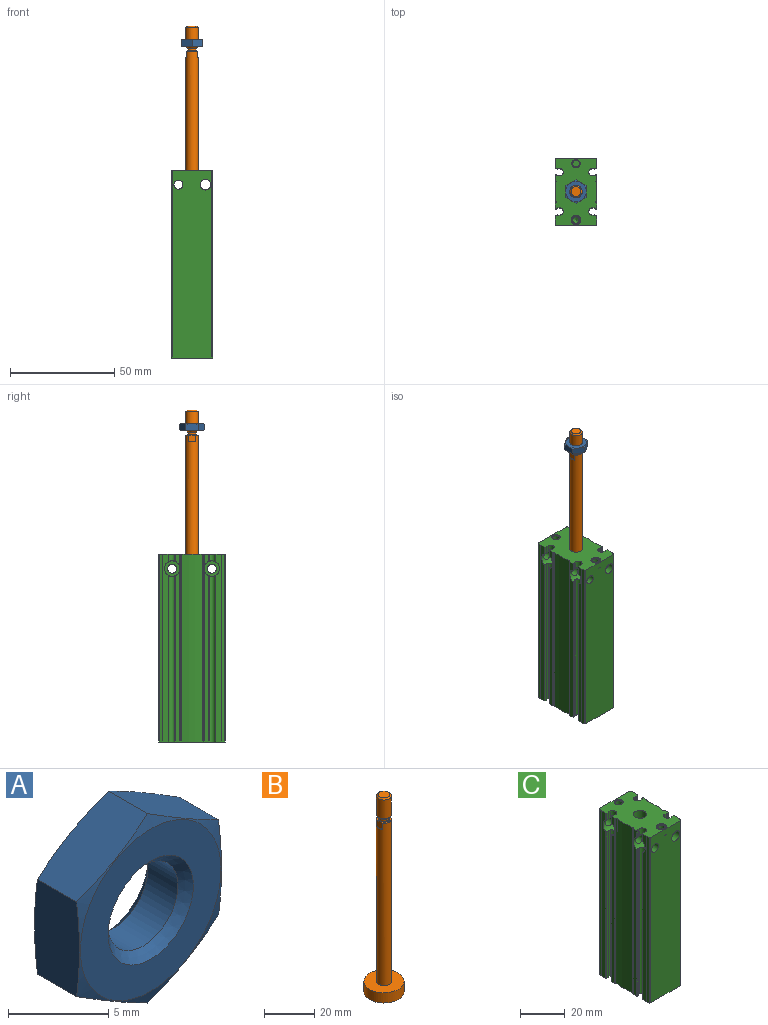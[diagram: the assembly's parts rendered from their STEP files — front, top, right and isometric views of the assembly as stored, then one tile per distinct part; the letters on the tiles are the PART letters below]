
ASSEMBLY  parts=3 mates=4
PART A: 13 faces, bbox 11.5x3.2x11.5 mm
  f0: plane 5.78x3.18mm, normal (-1,0,0), area 17.5mm2, adj f1,f2,f4,f8
  f1: plane 5x3.18mm, normal (-0.5,0,-0.87), area 17.5mm2, adj f0,f2,f8,f12
  f2: cone r=10.92mm half-angle=75deg, axis (0,1,0), area 10mm2, adj f0,f1,f3,f4,f5,f6,f12
  f3: plane 5.78x3.18mm, normal (1,0,0), area 17.5mm2, adj f2,f6,f8,f12
  f4: plane 5x3.18mm, normal (-0.5,0,0.87), area 17.5mm2, adj f0,f2,f6,f8
  f5: plane 9.9x9.9mm, normal (0,-1,0), area 48.7mm2, adj f2,f9
  f6: plane 5x3.18mm, normal (0.5,0,0.87), area 17.5mm2, adj f2,f3,f4,f8
  f7: plane 9.9x9.9mm, normal (0,1,0), area 48.7mm2, adj f8,f11
  f8: cone r=4.95mm half-angle=75deg, axis (0,-1,0), area 10mm2, adj f0,f1,f3,f4,f6,f7,f12
  f9: cone r=2.46mm half-angle=45deg, axis (0,-1,0), area 13.1mm2, adj f5,f10
  f10: cylinder r=2.46mm len=4.92mm, axis (0,1,0), area 32.7mm2, adj f9,f11
  f11: cone r=3mm half-angle=45deg, axis (0,1,0), area 13.1mm2, adj f7,f10
  f12: plane 5x3.18mm, normal (0.5,0,-0.87), area 17.5mm2, adj f1,f2,f3,f8
PART B: 16 faces, bbox 16x16x96.4 mm
  f0: torus R=2.2mm, axis (0,0,-1), area 4.1mm2, adj f1,f8
  f1: cylinder r=2mm len=4mm, axis (0,0,1), area 11.8mm2, adj f0,f2
  f2: torus R=2.2mm, axis (0,0,-1), area 2mm2, adj f1,f3
  f3: cone r=3mm half-angle=45deg, axis (0,0,1), area 21.2mm2, adj f2,f4
  f4: cylinder r=3mm len=9.16mm, axis (0,0,1), area 172.7mm2, adj f3,f5
  f5: cone r=2.39mm half-angle=45deg, axis (0,0,-1), area 14.7mm2, adj f4,f6
  f6: plane 4.77x4.77mm, normal (0,0,1), area 17.9mm2, adj f5
  f7: plane 16x16mm, normal (0,0,-1), area 201.1mm2, adj f11
  f8: plane 6x5mm, normal (0,0,1), area 10.8mm2, adj f0,f9,f12,f13
  f9: cylinder r=3mm len=79.4mm, axis (0,0,1), area 1475.6mm2, adj f8,f10,f12,f13,f14,f15
  f10: plane 16x16mm, normal (0,0,1), area 172.8mm2, adj f9,f11
  f11: cylinder r=8mm len=16mm, axis (0,0,1), area 251.3mm2, adj f7,f10
  f12: plane 3.32x3mm, normal (1,0,0), area 9.9mm2, adj f8,f9,f15
  f13: plane 3.32x3mm, normal (-1,0,0), area 9.9mm2, adj f8,f9,f14
  f14: plane 3.32x0.5mm, normal (0,0,1), area 1.1mm2, adj f9,f13
  f15: plane 3.32x0.5mm, normal (0,0,1), area 1.1mm2, adj f9,f12
PART C: 184 faces, bbox 20x32x90 mm
  f0: plane 7.43x3.25mm, normal (1,0,0), area 13.2mm2, adj f17,f79,f178,f180
  f1: plane 7.43x3.25mm, normal (1,0,0), area 13.2mm2, adj f23,f27,f178,f179
  f2: cylinder r=3.75mm len=7.5mm, axis (-1,0,0), area 83.1mm2, adj f3,f4,f5,f6,f7,f8,f9,f10
  f3: cylinder r=0.18mm len=79.59mm, axis (0,0,-1), area 22.5mm2, adj f2,f4,f92,f167
  f4: cylinder r=0.2mm len=79.71mm, axis (0,0,-1), area 26.5mm2, adj f2,f3,f5,f92
  f5: plane 79.76x0.95mm, normal (0.08,1,0), area 75.8mm2, adj f2,f4,f6,f92
  f6: cylinder r=1.8mm len=79.76mm, axis (0,0,-1), area 423.1mm2, adj f2,f5,f92,f157
  f7: plane 3.78x0.93mm, normal (-0.26,-0.96,0), area 3.5mm2, adj f2,f48,f134,f135
  f8: cylinder r=0.2mm len=79.77mm, axis (0,0,-1), area 26.5mm2, adj f2,f9,f92,f157
  f9: cylinder r=0.18mm len=79.68mm, axis (0,0,-1), area 22.5mm2, adj f2,f8,f92,f173
  f10: plane 3.71x1.07mm, normal (-0.17,-0.98,0), area 3.9mm2, adj f2,f48,f136,f174
  f11: cylinder r=0.2mm len=79.81mm, axis (0,0,-1), area 22.3mm2, adj f2,f62,f92,f173
  f12: cylinder r=6mm len=90mm, axis (0,0,-1), area 154.4mm2, adj f13,f48,f62,f92
  f13: cylinder r=0.43mm len=90mm, axis (0,0,-1), area 49.6mm2, adj f12,f48,f81,f92
  f14: cylinder r=0.43mm len=90mm, axis (0,0,-1), area 49.6mm2, adj f15,f48,f81,f92
  f15: cylinder r=6mm len=90mm, axis (0,0,-1), area 154.4mm2, adj f14,f48,f92,f110
  f16: cylinder r=0.2mm len=79.81mm, axis (0,0,-1), area 22.3mm2, adj f17,f74,f92,f110
  f17: cylinder r=3.75mm len=7.5mm, axis (-1,0,0), area 72.2mm2, adj f0,f16,f18,f19,f20,f21,f52,f66
  f18: cylinder r=3.75mm len=0.07mm, axis (-1,0,0), area 0mm2, adj f17,f21
  f19: cylinder r=0.18mm len=79.59mm, axis (0,0,-1), area 22.5mm2, adj f17,f20,f76,f92
  f20: plane 79.51x0.47mm, normal (-0.17,0.98,0), area 37.9mm2, adj f17,f19,f21,f92
  f21: cylinder r=0.2mm len=79.55mm, axis (0,0,-1), area 27.8mm2, adj f17,f18,f20,f66,f92
  f22: cylinder r=0.2mm len=79.55mm, axis (0,0,-1), area 27.8mm2, adj f23,f24,f92,f93,f139
  f23: cylinder r=3.75mm len=7.5mm, axis (-1,0,0), area 72.2mm2, adj f1,f22,f24,f57,f64,f93,f109,f111
  f24: cylinder r=3.75mm len=0.07mm, axis (-1,0,0), area 0mm2, adj f22,f23
  f25: cone r=2mm half-angle=60deg, axis (0,0,1), area 14.5mm2, adj f26
  f26: cylinder r=2mm len=53.5mm, axis (0,0,1), area 670.4mm2, adj f25,f27,f42
  f27: cylinder r=2.15mm len=8mm, axis (-1,0,0), area 106.1mm2, adj f1,f26,f28,f177,f178,f179
  f28: plane 7.5x7.5mm, normal (-1,0,0), area 29.7mm2, adj f27,f29
  f29: cylinder r=3.75mm len=7.5mm, axis (-1,0,0), area 83.1mm2, adj f28,f30,f31,f32,f33,f34,f35,f36
  f30: cylinder r=0.18mm len=79.59mm, axis (0,0,-1), area 22.5mm2, adj f29,f92,f125,f127
  f31: cylinder r=0.2mm len=79.55mm, axis (0,0,-1), area 27.8mm2, adj f29,f63,f92,f127
  f32: cylinder r=0.2mm len=79.81mm, axis (0,0,-1), area 22.3mm2, adj f29,f61,f92,f132
  f33: cylinder r=0.18mm len=79.68mm, axis (0,0,-1), area 22.5mm2, adj f29,f34,f92,f132
  f34: cylinder r=0.2mm len=79.77mm, axis (0,0,-1), area 26.5mm2, adj f29,f33,f39,f92
  f35: cylinder r=1.8mm len=79.76mm, axis (0,0,-1), area 423.1mm2, adj f29,f39,f92,f123
  f36: cylinder r=2.15mm len=4.3mm, axis (0,1,0), area 46.3mm2, adj f29,f60
  f37: cylinder r=2.15mm len=12.86mm, axis (0,1,0), area 173.7mm2, adj f2,f29
  f38: cylinder r=2.15mm len=4.3mm, axis (0,1,0), area 46.3mm2, adj f2,f81
  f39: plane 79.78x0.93mm, normal (-0.26,0.96,0), area 75.8mm2, adj f29,f34,f35,f92
  f40: plane 4.05x4.05mm, normal (0,0,1), area 3.3mm2, adj f41,f45
  f41: cone r=1.75mm half-angle=45deg, axis (0,0,1), area 3.6mm2, adj f40,f44
  f42: plane 4x4mm, normal (0,0,-1), area 2.9mm2, adj f26,f43
  f43: cone r=1.5mm half-angle=45deg, axis (0,0,-1), area 3.6mm2, adj f42,f44
  f44: cylinder r=1.5mm len=3mm, axis (0,0,1), area 28.3mm2, adj f41,f43
  f45: cone r=2.27mm half-angle=45deg, axis (0,0,-1), area 4.3mm2, adj f40,f46
  f46: cylinder r=2.25mm len=4.5mm, axis (0,0,1), area 0.4mm2, adj f45,f47
  f47: cone r=2.37mm half-angle=30deg, axis (0,0,1), area 3.3mm2, adj f46,f48
  f48: plane 32x20mm, normal (0,0,1), area 524.9mm2, adj f7,f10,f12,f13,f14,f15,f47,f49
  f49: cylinder r=3mm len=17.4mm, axis (0,0,1), area 328mm2, adj f48,f50
  f50: plane 16x16mm, normal (0,0,-1), area 172.8mm2, adj f49,f91
  f51: plane 90x0.28mm, normal (0.77,0.64,0), area 32.3mm2, adj f48,f56,f57,f92
  f52: cylinder r=0.2mm len=90mm, axis (0,0,-1), area 12.5mm2, adj f17,f48,f53,f66,f92,f108
  f53: plane 90x0.28mm, normal (0.77,-0.64,0), area 32.3mm2, adj f48,f52,f54,f92
  f54: cylinder r=0.75mm len=90mm, axis (0,0,-1), area 54mm2, adj f48,f53,f55,f92
  f55: cylinder r=47.5mm len=90mm, axis (0,0,-1), area 876.4mm2, adj f48,f54,f56,f92
  f56: cylinder r=0.75mm len=90mm, axis (0,0,-1), area 54mm2, adj f48,f51,f55,f92
  f57: cylinder r=0.2mm len=90mm, axis (0,0,-1), area 12.5mm2, adj f23,f48,f51,f64,f92,f93
  f58: cylinder r=0.2mm len=90mm, axis (0,0,-1), area 12.5mm2, adj f29,f48,f59,f63,f92,f166
  f59: plane 6.26x2.2mm, normal (-1,0,0), area 9.8mm2, adj f29,f48,f58,f128
  f60: plane 90x18.69mm, normal (0,-1,0), area 1647.2mm2, adj f36,f48,f92,f117,f118,f179
  f61: plane 90x2.52mm, normal (-1,0,0), area 219mm2, adj f29,f32,f48,f92,f119,f121
  f62: plane 90x2.52mm, normal (-1,0,0), area 219mm2, adj f2,f11,f12,f48,f92,f174
  f63: plane 82.26x2.2mm, normal (-1,0,0), area 177.3mm2, adj f29,f31,f58,f92
  f64: plane 6.26x2.2mm, normal (1,0,0), area 9.8mm2, adj f23,f48,f57,f133
  f65: plane 6.26x2.2mm, normal (-1,0,0), area 9.8mm2, adj f2,f48,f159,f161
  f66: plane 82.26x2.2mm, normal (1,0,0), area 177.3mm2, adj f17,f21,f52,f92
  f67: cylinder r=0.18mm len=3.68mm, axis (0,0,-1), area 1mm2, adj f17,f48,f138,f168
  f68: cylinder r=0.18mm len=79.68mm, axis (0,0,-1), area 22.5mm2, adj f17,f69,f74,f92
  f69: cylinder r=0.2mm len=79.77mm, axis (0,0,-1), area 26.5mm2, adj f17,f68,f70,f92
  f70: plane 79.78x0.93mm, normal (0.26,-0.96,0), area 75.8mm2, adj f17,f69,f71,f92
  f71: cylinder r=1.8mm len=79.76mm, axis (0,0,-1), area 423.6mm2, adj f17,f70,f72,f92
  f72: plane 79.76x0.95mm, normal (-0.08,1,0), area 75.8mm2, adj f17,f71,f76,f92
  f73: plane 3.76x0.95mm, normal (-0.08,1,0), area 3.6mm2, adj f17,f48,f75,f137
  f74: plane 79.71x1.07mm, normal (0.17,-0.98,0), area 85.8mm2, adj f16,f17,f68,f92
  f75: cylinder r=0.2mm len=3.71mm, axis (0,0,-1), area 1.2mm2, adj f17,f48,f73,f77
  f76: cylinder r=0.2mm len=79.71mm, axis (0,0,-1), area 26.5mm2, adj f17,f19,f72,f92
  f77: cylinder r=0.18mm len=3.59mm, axis (0,0,-1), area 1mm2, adj f17,f48,f75,f175
  f78: plane 7.43x3.25mm, normal (1,0,0), area 13.2mm2, adj f17,f79,f178,f180
  f79: cylinder r=2.15mm len=8mm, axis (-1,0,0), area 108.1mm2, adj f0,f78,f80,f178,f180
  f80: plane 7.5x7.5mm, normal (-1,0,0), area 29.7mm2, adj f2,f79
  f81: plane 90x18.69mm, normal (0,1,0), area 1607.9mm2, adj f13,f14,f38,f48,f82,f92,f99,f180
  f82: cone r=2.5mm half-angle=45deg, axis (0,1,0), area 8.8mm2, adj f81,f83
  f83: cylinder r=2.07mm len=5.57mm, axis (0,1,0), area 72.3mm2, adj f82,f100
  f84: plane 13.4x13.4mm, normal (0,0,-1), area 141mm2, adj f86
  f85: cone r=9.4mm half-angle=45deg, axis (0,0,-1), area 32.7mm2, adj f89,f92
  f86: cone r=7mm half-angle=45deg, axis (0,0,1), area 18.3mm2, adj f84,f87
  f87: cylinder r=7mm len=14mm, axis (0,0,1), area 79.2mm2, adj f86,f88
  f88: plane 18x18mm, normal (0,0,-1), area 100.5mm2, adj f87,f89
  f89: cylinder r=9mm len=18mm, axis (0,0,1), area 96.1mm2, adj f85,f88
  f90: plane 16x16mm, normal (0,0,1), area 201.1mm2, adj f91
  f91: cylinder r=8mm len=55mm, axis (0,0,1), area 2764.6mm2, adj f50,f90
  f92: plane 32x20mm, normal (0,0,-1), area 280.5mm2, adj f3,f4,f5,f6,f8,f9,f11,f12
  f93: plane 82.26x2.2mm, normal (1,0,0), area 177.3mm2, adj f22,f23,f57,f92
  f94: cone r=1.62mm half-angle=45deg, axis (0,0,-1), area 6.1mm2, adj f92,f95
  f95: cylinder r=1.62mm len=7.12mm, axis (0,0,1), area 72.5mm2, adj f94,f96
  f96: plane 3.24x3.24mm, normal (0,0,-1), area 8.3mm2, adj f95
  f97: plane 4.13x4.13mm, normal (0,1,0), area 13.4mm2, adj f98
  f98: cylinder r=2.07mm len=5.57mm, axis (0,1,0), area 72.3mm2, adj f97,f99
  f99: cone r=2.5mm half-angle=45deg, axis (0,1,0), area 8.8mm2, adj f81,f98
  f100: plane 4.13x4.13mm, normal (0,1,0), area 13.4mm2, adj f83
  f101: plane 3.24x3.24mm, normal (0,0,-1), area 8.3mm2, adj f102
  f102: cylinder r=1.62mm len=7.12mm, axis (0,0,1), area 72.5mm2, adj f101,f103
  f103: cone r=1.62mm half-angle=45deg, axis (0,0,-1), area 6.1mm2, adj f92,f102
  f104: cone r=2mm half-angle=45deg, axis (0,0,1), area 6.1mm2, adj f48,f105
  f105: cylinder r=1.62mm len=7.12mm, axis (0,0,1), area 72.5mm2, adj f104,f106
  f106: plane 3.24x3.24mm, normal (0,0,1), area 8.3mm2, adj f105
  f107: plane 82.26x2.2mm, normal (-1,0,0), area 177.3mm2, adj f2,f92,f158,f161
  f108: plane 6.26x2.2mm, normal (1,0,0), area 9.8mm2, adj f17,f48,f52,f176
  f109: plane 90x2.52mm, normal (1,0,0), area 219mm2, adj f23,f48,f92,f113,f116,f120
  f110: plane 90x2.52mm, normal (1,0,0), area 219mm2, adj f15,f16,f17,f48,f92,f160
  f111: plane 79.71x1.07mm, normal (0.17,0.98,0), area 85.8mm2, adj f23,f92,f120,f147
  f112: plane 79.78x0.93mm, normal (0.26,0.96,0), area 75.8mm2, adj f23,f92,f145,f146
  f113: cylinder r=6mm len=90mm, axis (0,0,-1), area 154.4mm2, adj f48,f92,f109,f118
  f114: plane 3.71x1.07mm, normal (0.17,0.98,0), area 3.9mm2, adj f23,f48,f116,f148
  f115: plane 79.76x0.95mm, normal (-0.08,-1,0), area 75.8mm2, adj f23,f92,f143,f145
  f116: cylinder r=0.2mm len=3.81mm, axis (0,0,-1), area 1mm2, adj f23,f48,f109,f114
  f117: cylinder r=0.43mm len=90mm, axis (0,0,-1), area 49.6mm2, adj f48,f60,f92,f119
  f118: cylinder r=0.43mm len=90mm, axis (0,0,-1), area 49.6mm2, adj f48,f60,f92,f113
  f119: cylinder r=6mm len=90mm, axis (0,0,-1), area 154.4mm2, adj f48,f61,f92,f117
  f120: cylinder r=0.2mm len=79.81mm, axis (0,0,-1), area 22.3mm2, adj f23,f92,f109,f111
  f121: cylinder r=0.2mm len=3.81mm, axis (0,0,-1), area 1mm2, adj f29,f48,f61,f122
  f122: plane 3.71x1.07mm, normal (-0.17,0.98,0), area 3.9mm2, adj f29,f48,f121,f149
  f123: plane 79.76x0.95mm, normal (0.08,-1,0), area 75.8mm2, adj f29,f35,f92,f125
  f124: cylinder r=0.2mm len=3.71mm, axis (0,0,-1), area 1.2mm2, adj f29,f48,f126,f130
  f125: cylinder r=0.2mm len=79.71mm, axis (0,0,-1), area 26.5mm2, adj f29,f30,f92,f123
  f126: cylinder r=0.18mm len=3.59mm, axis (0,0,-1), area 1mm2, adj f29,f48,f124,f129
  f127: plane 79.51x0.47mm, normal (0.17,-0.98,0), area 37.9mm2, adj f29,f30,f31,f92
  f128: cylinder r=0.2mm len=3.55mm, axis (0,0,-1), area 1.2mm2, adj f29,f48,f59,f129
  f129: plane 3.51x0.47mm, normal (0.17,-0.98,0), area 1.7mm2, adj f29,f48,f126,f128
  f130: plane 3.76x0.95mm, normal (0.08,-1,0), area 3.6mm2, adj f29,f48,f124,f151
  f131: plane 3.78x0.93mm, normal (-0.26,0.96,0), area 3.5mm2, adj f29,f48,f150,f151
  f132: plane 79.71x1.07mm, normal (-0.17,0.98,0), area 85.8mm2, adj f29,f32,f33,f92
  f133: cylinder r=0.2mm len=3.55mm, axis (0,0,-1), area 1.2mm2, adj f23,f48,f64,f154
  f134: cylinder r=1.8mm len=3.76mm, axis (0,0,-1), area 19.7mm2, adj f2,f7,f48,f172
  f135: cylinder r=0.2mm len=3.77mm, axis (0,0,-1), area 1.2mm2, adj f2,f7,f48,f136
  f136: cylinder r=0.18mm len=3.68mm, axis (0,0,-1), area 1mm2, adj f2,f10,f48,f135
  f137: cylinder r=1.8mm len=3.76mm, axis (0,0,-1), area 19.7mm2, adj f17,f48,f73,f156
  f138: cylinder r=0.2mm len=3.77mm, axis (0,0,-1), area 1.2mm2, adj f17,f48,f67,f156
  f139: plane 79.51x0.47mm, normal (-0.17,-0.98,0), area 37.9mm2, adj f22,f23,f92,f141
  f140: cylinder r=0.18mm len=3.59mm, axis (0,0,-1), area 1mm2, adj f23,f48,f142,f154
  f141: cylinder r=0.18mm len=79.59mm, axis (0,0,-1), area 22.5mm2, adj f23,f92,f139,f143
  f142: cylinder r=0.2mm len=3.71mm, axis (0,0,-1), area 1.2mm2, adj f23,f48,f140,f144
  f143: cylinder r=0.2mm len=79.71mm, axis (0,0,-1), area 26.5mm2, adj f23,f92,f115,f141
  f144: plane 3.76x0.95mm, normal (-0.08,-1,0), area 3.6mm2, adj f23,f48,f142,f153
  f145: cylinder r=1.8mm len=79.76mm, axis (0,0,-1), area 423.6mm2, adj f23,f92,f112,f115
  f146: cylinder r=0.2mm len=79.77mm, axis (0,0,-1), area 26.5mm2, adj f23,f92,f112,f147
  f147: cylinder r=0.18mm len=79.68mm, axis (0,0,-1), area 22.5mm2, adj f23,f92,f111,f146
  f148: cylinder r=0.18mm len=3.68mm, axis (0,0,-1), area 1mm2, adj f23,f48,f114,f152
  f149: cylinder r=0.18mm len=3.68mm, axis (0,0,-1), area 1mm2, adj f29,f48,f122,f150
  f150: cylinder r=0.2mm len=3.77mm, axis (0,0,-1), area 1.2mm2, adj f29,f48,f131,f149
  f151: cylinder r=1.8mm len=3.76mm, axis (0,0,-1), area 19.7mm2, adj f29,f48,f130,f131
  f152: cylinder r=0.2mm len=3.77mm, axis (0,0,-1), area 1.2mm2, adj f23,f48,f148,f155
  f153: cylinder r=1.8mm len=3.76mm, axis (0,0,-1), area 19.7mm2, adj f23,f48,f144,f155
  f154: plane 3.51x0.47mm, normal (-0.17,-0.98,0), area 1.7mm2, adj f23,f48,f133,f140
  f155: plane 3.78x0.93mm, normal (0.26,0.96,0), area 3.5mm2, adj f23,f48,f152,f153
  f156: plane 3.78x0.93mm, normal (0.26,-0.96,0), area 3.5mm2, adj f17,f48,f137,f138
  f157: plane 79.78x0.93mm, normal (-0.26,-0.96,0), area 75.8mm2, adj f2,f6,f8,f92
  f158: cylinder r=0.2mm len=79.55mm, axis (0,0,-1), area 27.8mm2, adj f2,f92,f107,f167
  f159: cylinder r=0.2mm len=3.55mm, axis (0,0,-1), area 1.2mm2, adj f2,f48,f65,f169
  f160: cylinder r=0.2mm len=3.81mm, axis (0,0,-1), area 1mm2, adj f17,f48,f110,f168
  f161: cylinder r=0.2mm len=90mm, axis (0,0,-1), area 12.5mm2, adj f2,f48,f65,f92,f107,f162
  f162: plane 90x0.28mm, normal (-0.77,-0.64,0), area 32.3mm2, adj f48,f92,f161,f163
  f163: cylinder r=0.75mm len=90mm, axis (0,0,-1), area 54mm2, adj f48,f92,f162,f164
  f164: cylinder r=47.5mm len=90mm, axis (0,0,-1), area 876.4mm2, adj f48,f92,f163,f165
  f165: cylinder r=0.75mm len=90mm, axis (0,0,-1), area 54mm2, adj f48,f92,f164,f166
  f166: plane 90x0.28mm, normal (-0.77,0.64,0), area 32.3mm2, adj f48,f58,f92,f165
  f167: plane 79.51x0.47mm, normal (0.17,0.98,0), area 37.9mm2, adj f2,f3,f92,f158
  f168: plane 3.71x1.07mm, normal (0.17,-0.98,0), area 3.9mm2, adj f17,f48,f67,f160
  f169: plane 3.51x0.47mm, normal (0.17,0.98,0), area 1.7mm2, adj f2,f48,f159,f170
  f170: cylinder r=0.18mm len=3.59mm, axis (0,0,-1), area 1mm2, adj f2,f48,f169,f171
  f171: cylinder r=0.2mm len=3.71mm, axis (0,0,-1), area 1.2mm2, adj f2,f48,f170,f172
  f172: plane 3.76x0.95mm, normal (0.08,1,0), area 3.6mm2, adj f2,f48,f134,f171
  f173: plane 79.71x1.07mm, normal (-0.17,-0.98,0), area 85.8mm2, adj f2,f9,f11,f92
  f174: cylinder r=0.2mm len=3.81mm, axis (0,0,-1), area 1mm2, adj f2,f10,f48,f62
  f175: plane 3.51x0.47mm, normal (-0.17,0.98,0), area 1.7mm2, adj f17,f48,f77,f176
  f176: cylinder r=0.2mm len=3.55mm, axis (0,0,-1), area 1.2mm2, adj f17,f48,f108,f175
  f177: plane 7.43x3.25mm, normal (1,0,0), area 13.2mm2, adj f23,f27,f178,f179
  f178: cylinder r=2.55mm len=14.82mm, axis (0,-1,0), area 203mm2, adj f0,f1,f17,f23,f27,f78,f79,f177
  f179: cylinder r=2.55mm len=5.1mm, axis (0,-1,0), area 53.3mm2, adj f1,f23,f27,f60,f177
  f180: cylinder r=2.55mm len=5.1mm, axis (0,-1,0), area 53.4mm2, adj f0,f17,f78,f79,f81
  f181: cone r=2.02mm half-angle=45deg, axis (0,0,1), area 4.3mm2, adj f182,f183
  f182: plane 4.5x4.5mm, normal (0,0,1), area 3mm2, adj f181,f183
  f183: cylinder r=2.25mm len=4.5mm, axis (0,0,1), area 3.2mm2, adj f181,f182
PLACE A rot(axis=(1,0,0),90deg) t=(32.05,23.75,-52.29)mm
PLACE B t=(32.05,23.75,-57.71)mm
PLACE C t=(32.05,23.75,-114.71)mm
MATE planar A.f2 <-> B.f0  axis (0,0,-1) through (32.05,23.75,-55.49)mm
MATE cylindrical A.f2 <-> B.f0  axis (0,0,1) through (32.05,23.75,-52.83)mm
MATE cylindrical C.f49 <-> B.f0  axis (0,0,1) through (32.05,23.75,-123.41)mm
MATE planar B.f0 <-> C.f49  axis (0,0,1) through (32.05,23.75,-137.11)mm
